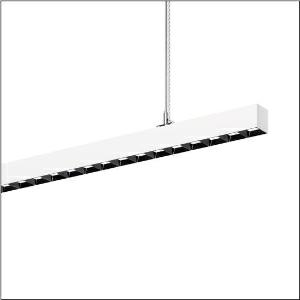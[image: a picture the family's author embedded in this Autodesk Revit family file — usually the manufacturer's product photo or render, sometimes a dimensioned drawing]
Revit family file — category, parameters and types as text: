
# Revit family: silica_r__21_51mx32dc4dwb_0a61
name_source: partatom
category: Lighting Fixtures
units: mm (PartAtom-declared; Revit-internal decimal feet)

## family parameters
Cut with Voids When Loaded = No
Host = Face
Light Source = No
Part Type = Normal
Room Calculation Point = No
Round Connector Dimension = Use Diameter
Shared = No

## types (1)
- --- (1 x LED, 18230 lm, 105.8 W, 4000K)
    Apparent Load = 106 VA
    CIE Flux Codes = 86 99 100 59 100
    Color Rendering = 80
    Color Temperature = 4000K
    Default Elevation = 1800 mm
    Description = Silica® 21, office luminaire, primary light control with darklight reflector, of PMMA, black, CAT 2 (L<= 3000cd/m²), light emission: direct/indirect distribution, primary light characteristic: symmetric, installation type: suspended mounting, LED, rated luminous flux: 18.230lm, luminous efficacy: 172lm/W, light colour: 840, colour temperature: 4000K, with terminal, 3+2-pole, max. 2.5mm², mains connection: 220..240V, AC, 50/60Hz, rated input power: 105.8W, luminaire housing, of aluminium, traffic white (RAL 9016), length: 3.004mm, width: 53mm, height: 53mm, protection rating (complete): IP20, insulation class (complete): insulation class I (protective earthing), certification: CE, permissible operating ambient temperature: 0..+35°C, standard: EN 50419, packaging unit: 1 piece
    Height = 53 mm
    Lamp = 1 x LED
    Lamp Light Flux = 18230 lm
    Lamp Power = 105.8 W
    Lamp count = 1
    Length = 3004 mm
    Luminous efficacy = 172 lm/W
    Manufacturer = Siteco
    ModVariant = No
    Model = 51MX32DC4DWB
    Mounting Place = Ceiling
    Mounting Type = Pendant
    Number of Poles = 1
    OnlyDefault = Yes
    Power Factor = 1
    Product Name = Silica® 21
    Product group = office luminaire | ceiling pendant
    ProductGroupID = 902
    Protection Class = Protection class I
    Protection Degree = IP 20
    RLX_Detail_Level = 1
    RLX_Emergency_Light_Flux = 0 lm
    RLX_Emergency_Type = 0
    RLX_Emergency_Type_DB = No
    RlxData = <blob elided: 66713 chars, md5=5d50d066>
    Socket = socket
    Standby Power = 0 W
    System Light Flux = 18230 lm
    System Power = 106 W
    Type Comments = factory setting: luminous flux: 100 % | dim-lin: 254 | 366 mA
    Type Image = l_1313619.jpg
    URL = http://relux.com
    VarID = @adj_071089
    Voltage = 0 V
    Weight = 0.00 kg
    Width = 53 mm

## geometry (parser evidence)
native form markers: Blend x4, Sweep x12
no freeform markers — native parametric forms only
